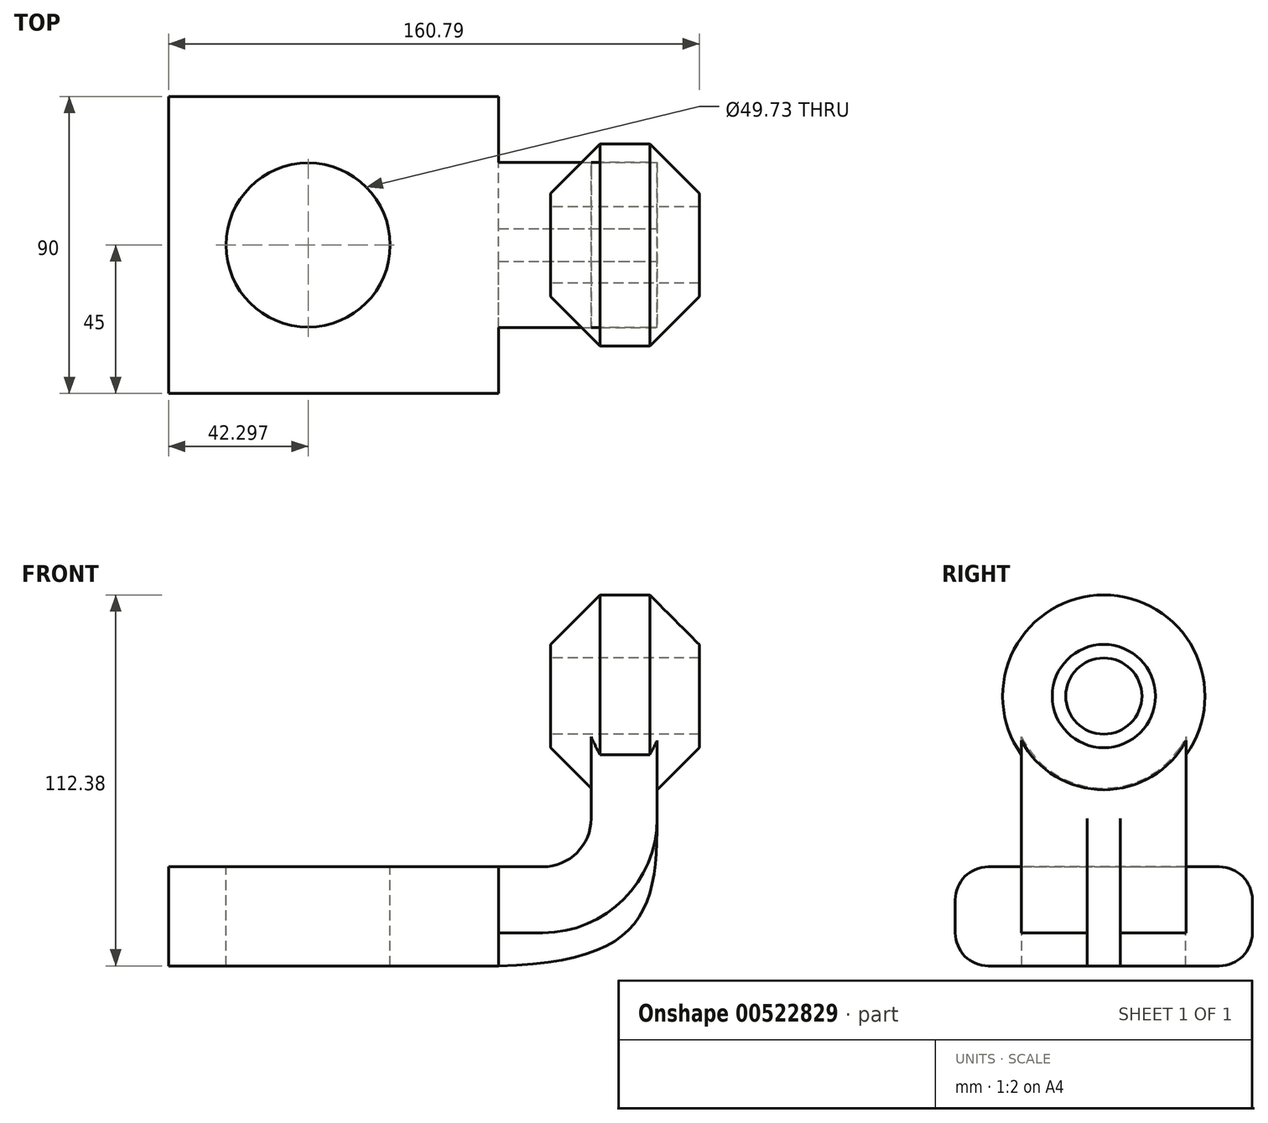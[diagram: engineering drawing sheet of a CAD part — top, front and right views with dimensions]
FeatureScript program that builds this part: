
annotation { "Feature Type Name" : "Feature", "Feature Type Description" : "" }
export const myFeature = defineFeature(function(context is Context, id is Id, definition is map)
    precondition{}
    {
        {
            var Q0;
            Q0=qCreatedBy(makeId("Front.planeOp"),FACE);
            var sketch = newSketch(context, id + "F0", { "sketchPlane" : qUnion([Q0])});
            skLineSegment(sketch, "E0.bottom", {"start": v(50, -15) * mm, "end": v(-50, -15) * mm});
            skLineSegment(sketch, "E0.top", {"start": v(50, 15) * mm, "end": v(-50, 15) * mm});
            skLineSegment(sketch, "E0.left", {"start": v(50, -15) * mm, "end": v(50, 15) * mm});
            skLineSegment(sketch, "E0.right", {"start": v(-50, -15) * mm, "end": v(-50, 15) * mm});
            skPoint(sketch, "E0.middle", {"position": v(0, 0) * mm});
            skLineSegment(sketch, "E1.bottom", {"start": v(65.79, 38.6) * mm, "end": v(110.79, 38.6) * mm});
            skLineSegment(sketch, "E1.top", {"start": v(65.79, 97.38) * mm, "end": v(110.79, 97.38) * mm});
            skLineSegment(sketch, "E1.left", {"start": v(65.79, 38.6) * mm, "end": v(65.79, 97.38) * mm});
            skLineSegment(sketch, "E1.right", {"start": v(110.79, 38.6) * mm, "end": v(110.79, 97.38) * mm});
            skLineSegment(sketch, "E2", {"start": v(50, 15) * mm, "end": v(63.35, 15) * mm});
            skArc(sketch, "E3", {"start": v(63.35, 15) * mm, "mid": v(73.74, 19.3) * mm, "end": v(78.04, 29.69) * mm});
            skLineSegment(sketch, "E4", {"start": v(78.04, 29.69) * mm, "end": v(78.04, 66.74) * mm});
            skLineSegment(sketch, "E5.0", {"start": v(98.04, 29.69) * mm, "end": v(98.04, 66.74) * mm});
            skArc(sketch, "E5.1", {"start": v(63.35, -5) * mm, "mid": v(87.88, 5.16) * mm, "end": v(98.04, 29.69) * mm});
            skLineSegment(sketch, "E5.2", {"start": v(50, -5) * mm, "end": v(63.35, -5) * mm});
            skLineSegment(sketch, "E6", {"start": v(65.79, 66.74) * mm, "end": v(110.79, 66.74) * mm});
            skFitSpline(sketch, "E7", {"points": [v(50, -15) * mm, v(98.04, 29.69) * mm], "startDerivative": vector(129.46, 3.22) * mm, "endDerivative": vector(-0.42, 87.56) * mm});
            skLineSegment(sketch, "E8.bottom", {"start": v(110.79, 78.27) * mm, "end": v(65.79, 78.27) * mm});
            skLineSegment(sketch, "E8.top", {"start": v(110.79, 53.38) * mm, "end": v(65.79, 53.38) * mm});
            skLineSegment(sketch, "E8.left", {"start": v(110.79, 78.27) * mm, "end": v(110.79, 53.38) * mm});
            skLineSegment(sketch, "E8.right", {"start": v(65.79, 78.27) * mm, "end": v(65.79, 53.38) * mm});
            skLineSegment(sketch, "E9.bottom", {"start": v(-7.7, 34.89) * mm, "end": v(-32.57, 34.89) * mm});
            skLineSegment(sketch, "E9.top", {"start": v(-7.7, -33.76) * mm, "end": v(-32.57, -33.76) * mm});
            skLineSegment(sketch, "E9.left", {"start": v(-7.7, 34.89) * mm, "end": v(-7.7, -33.76) * mm});
            skLineSegment(sketch, "E9.right", {"start": v(-32.57, 34.89) * mm, "end": v(-32.57, -33.76) * mm});
            skSolve(sketch);
        }
        {
            var Q0;
            {var subQ3=sQuery(id+"F0.wireOp",EDGE,"E0.bottom");Q0=makeQuery(id+"F0.imprint","IMPRINT",FACE,{"disambiguationData":[TD([[makeQuery(id+"F0.imprint","IMPRINT",EDGE,{"derivedFrom":subQ3}),-1.0]])]});}
            var Q1;
            {var subQ4=sQuery(id+"F0.wireOp",EDGE,"E0.bottom");var subQ6=sQuery(id+"F0.wireOp",EDGE,"E9.left");var subQ8=makeQuery(id+"F0.imprint","INTERSECT",VERTEX,{"derivedFrom":[subQ4,subQ6]});Q1=makeQuery(id+"F0.imprint","IMPRINT",FACE,{"disambiguationData":[TD([[makeQuery(id+"F0.imprint","IMPRINT",EDGE,{"disambiguationData":[TD([[subQ8,1.0]])],"derivedFrom":subQ6}),1.0]])]});}
            extrude(context, id + "F1", {"entities" : qUnion([Q0, Q1]), "endBound" : BoundingType.SYMMETRIC, "depth" : 90 * mm, "offsetDistance" : 25 * mm});
        }
        {
            var Q0;
            {var subQ1=sQuery(id+"F0.wireOp",EDGE,"E2");Q0=makeQuery(id+"F0.imprint","IMPRINT",FACE,{"disambiguationData":[TD([[makeQuery(id+"F0.imprint","IMPRINT",EDGE,{"derivedFrom":subQ1}),-1.0]])]});}
            var Q1;
            {var subQ0=sQuery(id+"F0.wireOp",EDGE,"E4");var subQ1=sQuery(id+"F0.wireOp",EDGE,"E1.bottom");var subQ2=makeQuery(id+"F0.imprint","INTERSECT",VERTEX,{"derivedFrom":[subQ1,subQ0]});Q1=makeQuery(id+"F0.imprint","IMPRINT",FACE,{"disambiguationData":[TD([[makeQuery(id+"F0.imprint","IMPRINT",EDGE,{"disambiguationData":[TD([[subQ2,-1.0]])],"derivedFrom":subQ1}),1.0]])]});}
            extrude(context, id + "F2", {"entities" : qUnion([Q0, Q1]), "operationType" : NewBodyOperationType.ADD, "endBound" : BoundingType.SYMMETRIC, "depth" : 50 * mm, "offsetDistance" : 25 * mm});
        }
        {
            var Q0;
            Q0=makeQuery(id+"F0.imprint","IMPRINT",FACE,{"disambiguationData":[TD([[makeQuery(id+"F0.imprint","IMPRINT",EDGE,{"derivedFrom":sQuery(id+"F0.wireOp",EDGE,"E5.1")}),-1.0]])]});
            extrude(context, id + "F3", {"entities" : qUnion([Q0]), "operationType" : NewBodyOperationType.ADD, "endBound" : BoundingType.SYMMETRIC, "depth" : 10 * mm, "offsetDistance" : 25 * mm});
        }
        {
            var Q0;
            {var subQ4=sQuery(id+"F0.wireOp",EDGE,"E1.top");Q0=makeQuery(id+"F0.imprint","IMPRINT",FACE,{"disambiguationData":[TD([[makeQuery(id+"F0.imprint","IMPRINT",EDGE,{"derivedFrom":subQ4}),-1.0]])]});}
            var Q1;
            Q1=sQuery(id+"F0.wireOp",EDGE,"E6");
            revolve(context, id + "F4", {"operationType" : NewBodyOperationType.ADD, "entities" : qUnion([Q0]), "axis" : qUnion([Q1]), "revolveType" : RevolveType.FULL});
        }
        {
            var Q0;
            Q0=makeQuery(id+"F1.opExtrude","CAP_EDGE",EDGE,{"disambiguationData":[OSD([sQuery(id+"F0.wireOp",EDGE,"E0.top")])],"isStart":false});
            var Q1;
            Q1=makeQuery(id+"F1.opExtrude","CAP_EDGE",EDGE,{"disambiguationData":[OSD([sQuery(id+"F0.wireOp",EDGE,"E0.top")])],"isStart":true});
            var Q2;
            Q2=makeQuery(id+"F1.opExtrude","CAP_EDGE",EDGE,{"disambiguationData":[OSD([sQuery(id+"F0.wireOp",EDGE,"E0.bottom")])],"isStart":true});
            var Q3;
            Q3=makeQuery(id+"F1.opExtrude","CAP_EDGE",EDGE,{"disambiguationData":[OSD([sQuery(id+"F0.wireOp",EDGE,"E0.bottom")])],"isStart":false});
            fillet(context, id + "F5", {"entities" : qUnion([Q0, Q1, Q2, Q3]), "radius" : 10 * mm, "tangentPropagation" : true, "allowEdgeOverflow" : false});
        }
        {
            var Q0;
            {var subQ5=sQuery(id+"F0.wireOp",EDGE,"E9.bottom");Q0=makeQuery(id+"F0.imprint","IMPRINT",FACE,{"disambiguationData":[TD([[makeQuery(id+"F0.imprint","IMPRINT",EDGE,{"derivedFrom":subQ5}),1.0]])]});}
            var Q1;
            {var subQ5=sQuery(id+"F0.wireOp",EDGE,"E9.top");Q1=makeQuery(id+"F0.imprint","IMPRINT",FACE,{"disambiguationData":[TD([[makeQuery(id+"F0.imprint","IMPRINT",EDGE,{"derivedFrom":subQ5}),-1.0]])]});}
            var Q2;
            {var subQ0=sQuery(id+"F0.wireOp",EDGE,"E9.left");var subQ1=sQuery(id+"F0.wireOp",EDGE,"E0.bottom");var subQ2=makeQuery(id+"F0.imprint","INTERSECT",VERTEX,{"derivedFrom":[subQ1,subQ0]});Q2=makeQuery(id+"F0.imprint","IMPRINT",FACE,{"disambiguationData":[TD([[makeQuery(id+"F0.imprint","IMPRINT",EDGE,{"disambiguationData":[TD([[subQ2,-1.0]])],"derivedFrom":subQ1}),-1.0]])]});}
            var Q3;
            Q3=sQuery(id+"F0.wireOp",EDGE,"E9.left");
            revolve(context, id + "F6", {"entities" : qUnion([Q0, Q1, Q2]), "axis" : qUnion([Q3]), "revolveType" : RevolveType.FULL});
        }
        {
            var Q0;
            Q0=makeQuery(id+"F6.opRevolve","SWEPT_BODY",BODY,{"disambiguationData":[OSD([sQuery(id+"F0.wireOp",EDGE,"E9.bottom"),sQuery(id+"F0.wireOp",EDGE,"E9.top"),sQuery(id+"F0.wireOp",EDGE,"E9.left"),sQuery(id+"F0.wireOp",EDGE,"E9.right")])]});
            var Q1;
            Q1=makeQuery(id+"F1.opExtrude","SWEPT_BODY",BODY,{"disambiguationData":[OSD([sQuery(id+"F0.wireOp",EDGE,"E0.bottom"),sQuery(id+"F0.wireOp",EDGE,"E0.top"),sQuery(id+"F0.wireOp",EDGE,"E0.left"),sQuery(id+"F0.wireOp",EDGE,"E0.right")])]});
            booleanBodies(context, id + "F7", {"operationType" : BooleanOperationType.SUBTRACTION, "tools" : qUnion([Q0]), "targets" : qUnion([Q1])});
        }
        {
            var Q0;
            Q0=makeQuery(id+"F4.opRevolve","SWEPT_EDGE",EDGE,{"disambiguationData":[OSD([sQuery(id+"F0.wireOp",EDGE,"E1.top"),sQuery(id+"F0.wireOp",EDGE,"E1.left")])]});
            var Q1;
            Q1=makeQuery(id+"F4.opRevolve","SWEPT_EDGE",EDGE,{"disambiguationData":[OSD([sQuery(id+"F0.wireOp",EDGE,"E1.top"),sQuery(id+"F0.wireOp",EDGE,"E1.right")])]});
            chamfer(context, id + "F8", {"entities" : qUnion([Q0, Q1]), "width" : 15 * mm, "tangentPropagation" : true});
        }
    });
